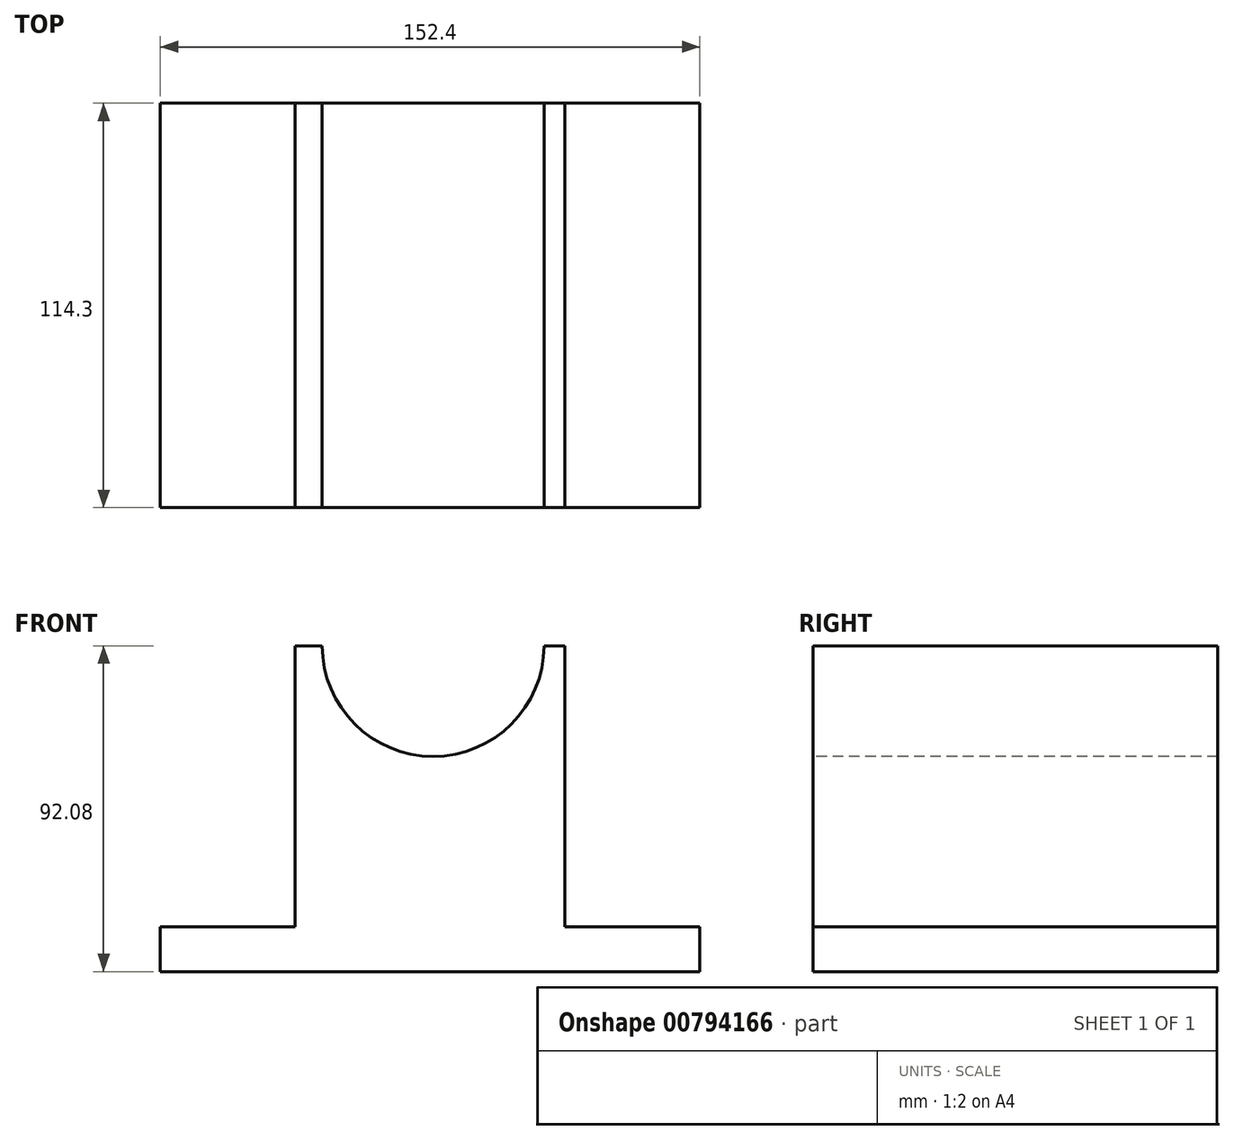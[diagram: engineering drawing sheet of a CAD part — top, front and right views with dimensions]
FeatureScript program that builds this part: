
annotation { "Feature Type Name" : "Feature", "Feature Type Description" : "" }
export const myFeature = defineFeature(function(context is Context, id is Id, definition is map)
    precondition{}
    {
        {
            var Q0;
            Q0=qCreatedBy(makeId("Front.planeOp"),FACE);
            var sketch = newSketch(context, id + "F0", { "sketchPlane" : qUnion([Q0])});
            skLineSegment(sketch, "E0", {"start": v(0, 0) * mm, "end": v(152.4, 0) * mm});
            skLineSegment(sketch, "E1", {"start": v(152.4, 0) * mm, "end": v(152.4, 12.7) * mm});
            skLineSegment(sketch, "E2", {"start": v(152.4, 12.7) * mm, "end": v(114.3, 12.7) * mm});
            skLineSegment(sketch, "E3", {"start": v(114.3, 12.7) * mm, "end": v(114.3, 92.08) * mm});
            skLineSegment(sketch, "E4", {"start": v(114.3, 92.08) * mm, "end": v(38.1, 92.08) * mm});
            skLineSegment(sketch, "E5", {"start": v(38.1, 92.08) * mm, "end": v(38.1, 12.7) * mm});
            skLineSegment(sketch, "E6", {"start": v(38.1, 12.7) * mm, "end": v(0, 12.7) * mm});
            skLineSegment(sketch, "E7", {"start": v(0, 12.7) * mm, "end": v(0, 0) * mm});
            skSolve(sketch);
        }
        {
            var Q0;
            Q0=qSketchRegion(id+"F0",true);
            extrude(context, id + "F1", {"entities" : qUnion([Q0]), "depth" : 114.3 * mm, "offsetDistance" : 25.4 * mm});
        }
        {
            var Q0;
            Q0=makeQuery(id+"F1.opExtrude","CAP_FACE",FACE,{"disambiguationData":[OSD([sQuery(id+"F0.wireOp",EDGE,"E0"),sQuery(id+"F0.wireOp",EDGE,"E1"),sQuery(id+"F0.wireOp",EDGE,"E2"),sQuery(id+"F0.wireOp",EDGE,"E3"),sQuery(id+"F0.wireOp",EDGE,"E4"),sQuery(id+"F0.wireOp",EDGE,"E5"),sQuery(id+"F0.wireOp",EDGE,"E6"),sQuery(id+"F0.wireOp",EDGE,"E7")])],"isStart":false});
            var sketch = newSketch(context, id + "F2", { "sketchPlane" : qUnion([Q0])});
            skArc(sketch, "E8", {"start": v(45.72, 92.08) * mm, "mid": v(77.06, 60.8) * mm, "end": v(108.4, 92.08) * mm});
            skSolve(sketch);
        }
        {
            var Q0;
            {var subQ0=sQuery(id+"F2.wireOp",EDGE,"E8");Q0=makeQuery(id+"F2.imprint","IMPRINT",FACE,{"disambiguationData":[TD([[makeQuery(id+"F2.imprint","IMPRINT",EDGE,{"derivedFrom":subQ0}),1.0]])]});}
            extrude(context, id + "F3", {"entities" : qUnion([Q0]), "operationType" : NewBodyOperationType.REMOVE, "endBound" : BoundingType.UP_TO_NEXT, "oppositeDirection" : true, "depth" : 25.4 * mm, "offsetDistance" : 25.4 * mm});
        }
    });
